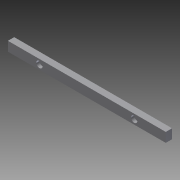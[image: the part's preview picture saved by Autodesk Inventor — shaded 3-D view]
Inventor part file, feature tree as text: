
AUTODESK INVENTOR PART (.ipt)
format: ipt  version: 2012 (Build 160160000, 160)  size: 83,456 bytes
history: native  units: in
note: dims shown in document units (in); Inventor stores cm internally (conversion verified against a paired STEP export)
features: extrude x2, sketch x2
ambient origin geometry x8: Origin, YZ Plane, XZ Plane, XY Plane, X Axis, Y Axis, Z Axis, Center Point
bodies: Solid1 (feature_tree)
feature tree (4):
  extrude  "Extrusion1"  Depth=1.5in
  extrude  "Extrusion2"  Depth=1.0in
  sketch  "Sketch1"  dims[d2=25.0in d3=1.5in]
  sketch  "Sketch2"  dims[d4=1.0in d5=1.0in d6=15.0in d7=5.0in d8=1.0in d9=0.0in d10=15.0in d11=5.0in d12=1.0in d13=1.0in d14=0.5in d15=0.0in]
